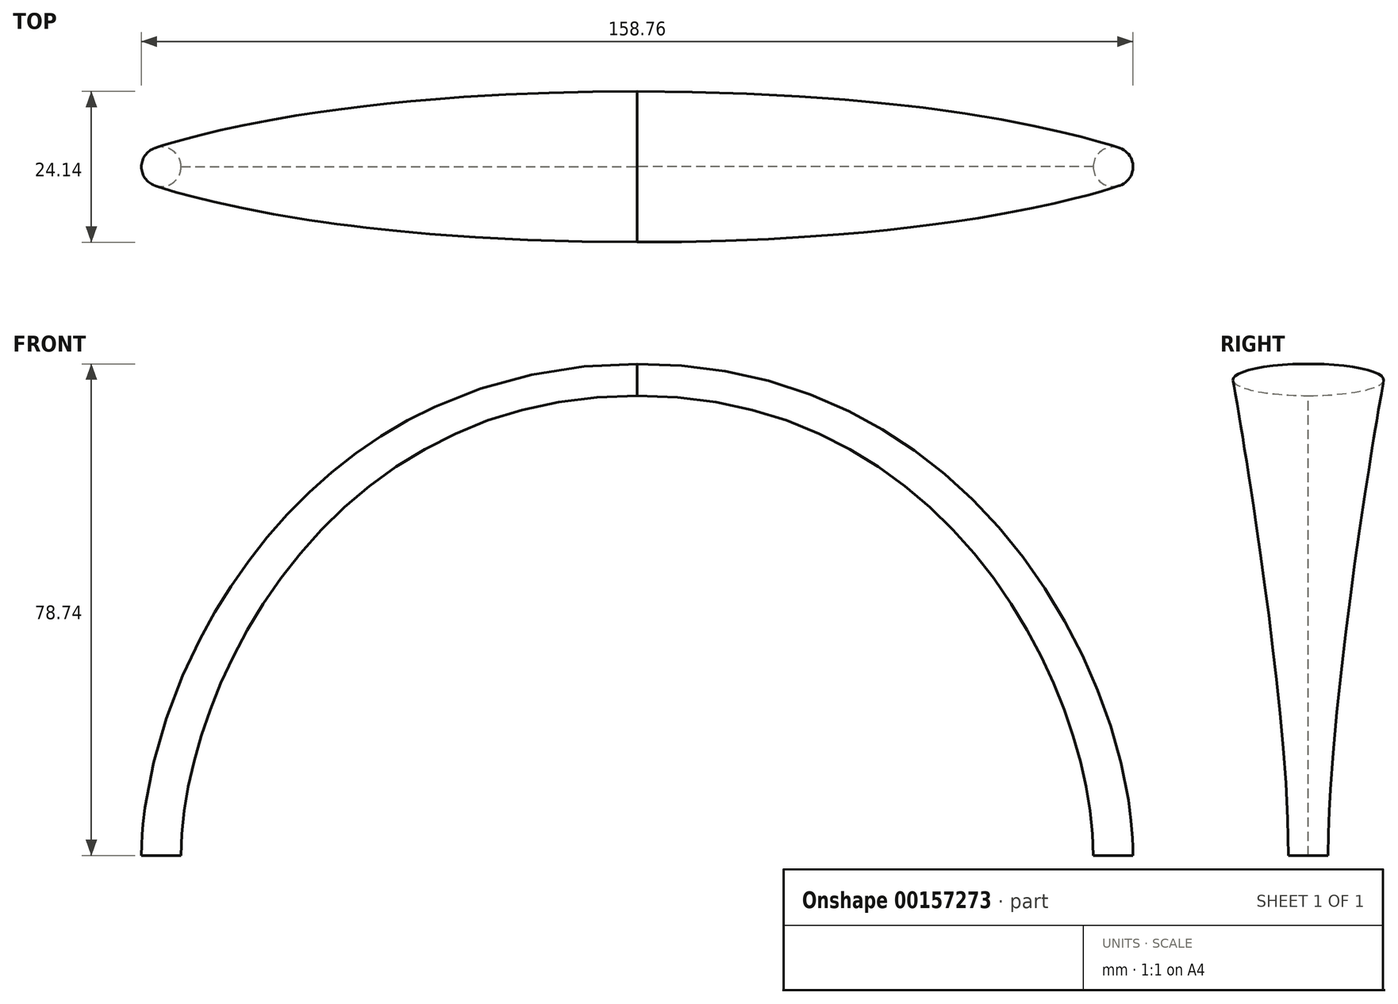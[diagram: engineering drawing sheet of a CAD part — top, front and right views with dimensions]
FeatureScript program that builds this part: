
annotation { "Feature Type Name" : "Feature", "Feature Type Description" : "" }
export const myFeature = defineFeature(function(context is Context, id is Id, definition is map)
    precondition{}
    {
        {
            var Q0;
            Q0=qCreatedBy(makeId("Top.planeOp"),FACE);
            var sketch = newSketch(context, id + "F0", { "sketchPlane" : qUnion([Q0])});
            skCircle(sketch, "E0", {"center": v(-76.2, 0) * mm, "radius": 3.18 * mm});
            skSolve(sketch);
        }
        {
            var Q0;
            Q0=qCreatedBy(makeId("Right.planeOp"),FACE);
            var sketch = newSketch(context, id + "F1", { "sketchPlane" : qUnion([Q0])});
            skEllipse(sketch, "E1", {"center": v(0, 76.2) * mm, "majorRadius": 12.07 * mm, "minorRadius": 2.54 * mm, "majorAxis": v(1, 0)});
            skSolve(sketch);
        }
        {
            var Q0;
            Q0 = qSketchRegion(id + "F0", true);
            var Q1;
            Q1 = qSketchRegion(id + "F1", true);
            loft(context, id + "F2", {"startCondition" : LoftEndDerivativeType.NORMAL_TO_PROFILE, "startMagnitude" : 1, "endCondition" : LoftEndDerivativeType.NORMAL_TO_PROFILE, "endMagnitude" : 2, "sheetProfilesArray" : [{ "sheetProfileEntities" : qUnion([Q0]) }, { "sheetProfileEntities" : qUnion([Q1]) }]});
        }
        {
            var Q0;
            Q0=makeQuery(id+"F2.opLoft","SWEPT_BODY",BODY,{"disambiguationData":[OSD([makeQuery(id+"F0.imprint","IMPRINT",FACE,{"disambiguationData":[TD([[makeQuery(id+"F0.imprint","IMPRINT",EDGE,{"derivedFrom":sQuery(id+"F0.wireOp",EDGE,"E0")}),1.0]])]}),makeQuery(id+"F1.imprint","IMPRINT",FACE,{"disambiguationData":[TD([[makeQuery(id+"F1.imprint","IMPRINT",EDGE,{"derivedFrom":sQuery(id+"F1.wireOp",EDGE,"E1")}),1.0]])]})])]});
            var Q1;
            Q1=qCreatedBy(makeId("Right.planeOp"),FACE);
            mirror(context, id + "F3", {"operationType" : NewBodyOperationType.ADD, "entities" : qUnion([Q0]), "mirrorPlane" : qUnion([Q1])});
        }
    });
